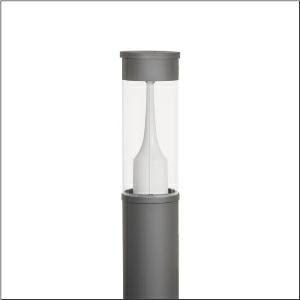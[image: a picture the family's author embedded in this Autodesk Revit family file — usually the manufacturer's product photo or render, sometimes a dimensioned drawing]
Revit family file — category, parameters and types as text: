
# Revit family: city-light_260_iq___st1_2a_5xa5295mf14h_84f0
name_source: partatom
category: Lighting Fixtures
units: mm (PartAtom-declared; Revit-internal decimal feet)

## family parameters
Cut with Voids When Loaded = No
Host = Face
Light Source = No
Part Type = Normal
Room Calculation Point = No
Round Connector Dimension = Use Diameter
Shared = No

## types (1)
- --- (1 x LED, 1540 lm, 11.8 W, 2700K)
    Apparent Load = 12 VA
    CIE Flux Codes = 22 61 93 96 100
    Color Rendering = 70
    Color Temperature = 2700K
    Default Elevation = 1800 mm
    Description = City-Light 260 iQ, light pillar, Module 540 iQ-SR, primary light control with 3 zone facetted reflector, of plastic, silver coated, highly specular, structured, primary optical cover: cover, of PMMA, transparent, partly coated, light distribution: ST1.2a, primary light characteristic: asymmetric, LED, High Power LED, rated luminous flux: 1.540lm, luminous efficacy: 131lm/W, light colour: 727, colour temperature: 2700K, control gear: ECG iQ, control: presetting dimming logarithmic, Street-Remote, Auto-Match, Temp-Guard, Lumen-Switch, Night-Set, Smart-Wire, Light-Fading, Desk-Remote (wireless, voltage-free reading and setting of iQ features in the workshop via application-optimized NFC function/RFID function), optimised constant luminous flux control (CLO 2.0), with terminal, 6-pole, max. 2.5mm², mains connection: 230..240V, AC, 50/60Hz, start of lifetime: 12W, end of service life: 12W, reduction: 6W, luminaire housing, cylindrical, of extruded aluminium section, coated, Siteco® metallic grey (DB 702S), length: 2.600mm, diameter: 200mm, Module 540 iQ-SR, traffic white (RAL 9016), equipment: standard, protection rating (complete): IP65, insulation class (complete): insulation class II (safety insulation), certification: CE, ENEC, VDE, packaging unit: 1 piece

Light Distribution: ST1.2a
    Height = 500 mm
    Lamp = 1 x LED
    Lamp Light Flux = 1540 lm
    Lamp Power = 11.8 W
    Lamp count = 1
    Length = 200 mm  [stored 0.656168 ft]
    Luminous efficacy = 131 lm/W
    Manufacturer = Siteco
    ModVariant = No
    Model = 5XA5295MF14H
    Mounting Place = Floor
    Mounting Type = Freestanding
    Number of Poles = 1
    OnlyDefault = Yes
    Power Factor = 1
    Product Name = City-Light 260 iQ | ST1.2a
    Product group = light pillar
    ProductGroupID = 1303
    Protection Class = Protection class II
    Protection Degree = IP 65
    RLX_Detail_Level = 1
    RLX_Emergency_Light_Flux = 0 lm
    RLX_Emergency_Type = 0
    RLX_Emergency_Type_DB = No
    RlxData = <blob elided: 60709 chars, md5=a5c073c7>
    Socket = socket
    Standby Power = 0 W
    System Light Flux = 1540 lm
    System Power = 12 W
    Type Comments = factory setting: luminous flux: 100 % | dim-lin: 254 | 472 mA
    Type Image = l_1006918.jpg
    URL = http://relux.com
    VarID = @adj_085391
    Voltage = 0 V
    Weight = 0.00 kg
    Width = 0 mm  [stored 0 ft]

note: [stored X ft] marks values corroborated as IEEE doubles in the binary element streams (Revit-internal decimal feet)

## geometry (parser evidence)
native form markers: Blend x4, Sweep x10
no freeform markers — native parametric forms only
